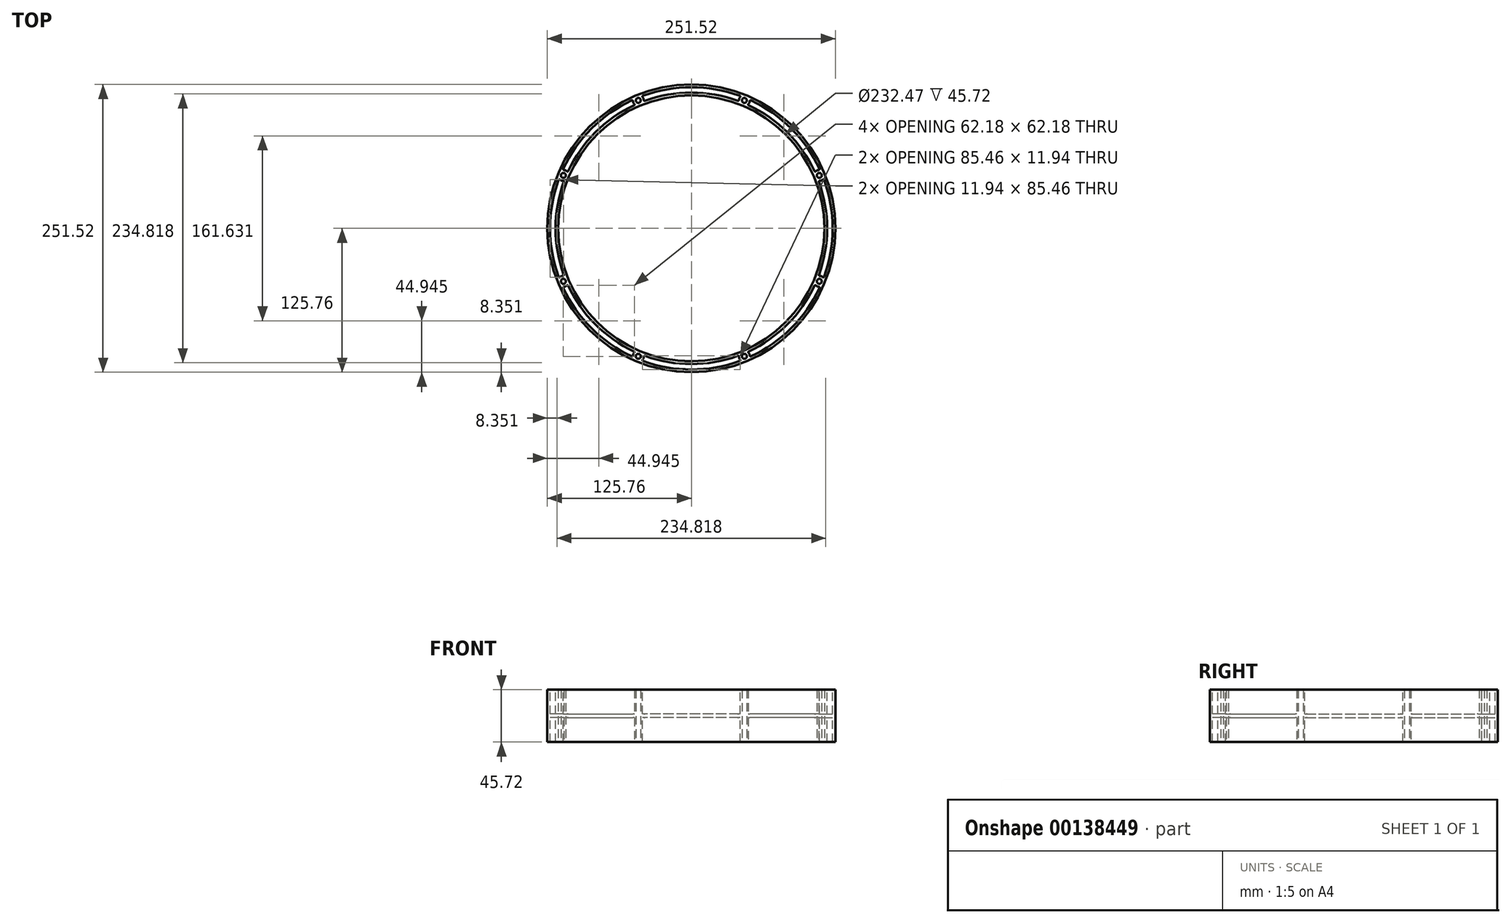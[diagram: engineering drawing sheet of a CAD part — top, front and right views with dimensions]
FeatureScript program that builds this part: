
annotation { "Feature Type Name" : "Feature", "Feature Type Description" : "" }
export const myFeature = defineFeature(function(context is Context, id is Id, definition is map)
    precondition{}
    {
        {
            var Q0;
            Q0=qCreatedBy(makeId("Top.planeOp"),FACE);
            var sketch = newSketch(context, id + "F0", { "sketchPlane" : qUnion([Q0])});
            skCircle(sketch, "E0", {"center": v(0, 0) * mm, "radius": 125.76 * mm});
            skCircle(sketch, "E1.cCircle", {"center": v(0, 0) * mm, "radius": 111.79 * mm, "construction": true});
            skLineSegment(sketch, "E1.0", {"start": v(46.3, -111.79) * mm, "end": v(-46.3, -111.79) * mm, "construction": true});
            skLineSegment(sketch, "E1.1", {"start": v(-46.3, -111.79) * mm, "end": v(-111.79, -46.3) * mm, "construction": true});
            skLineSegment(sketch, "E1.2", {"start": v(-111.79, -46.3) * mm, "end": v(-111.79, 46.3) * mm, "construction": true});
            skLineSegment(sketch, "E1.3", {"start": v(-111.79, 46.3) * mm, "end": v(-46.3, 111.79) * mm, "construction": true});
            skLineSegment(sketch, "E1.4", {"start": v(-46.3, 111.79) * mm, "end": v(46.3, 111.79) * mm, "construction": true});
            skLineSegment(sketch, "E1.5", {"start": v(46.3, 111.79) * mm, "end": v(111.79, 46.3) * mm, "construction": true});
            skLineSegment(sketch, "E1.6", {"start": v(111.79, 46.3) * mm, "end": v(111.79, -46.3) * mm, "construction": true});
            skLineSegment(sketch, "E1.7", {"start": v(111.79, -46.3) * mm, "end": v(46.3, -111.79) * mm, "construction": true});
            skCircle(sketch, "E2", {"center": v(-46.3, 111.79) * mm, "radius": 4.76 * mm, "construction": true});
            skCircle(sketch, "E3", {"center": v(0, 0) * mm, "radius": 116.24 * mm});
            skCircle(sketch, "E4", {"center": v(-46.3, 111.79) * mm, "radius": 2.15 * mm});
            skCircle(sketch, "E5", {"center": v(46.3, 111.79) * mm, "radius": 2.15 * mm});
            skCircle(sketch, "E6", {"center": v(111.79, 46.3) * mm, "radius": 2.15 * mm});
            skCircle(sketch, "E7", {"center": v(111.79, -46.3) * mm, "radius": 2.15 * mm});
            skCircle(sketch, "E8", {"center": v(46.3, -111.79) * mm, "radius": 2.15 * mm});
            skCircle(sketch, "E9", {"center": v(-46.3, -111.79) * mm, "radius": 2.15 * mm});
            skCircle(sketch, "E10", {"center": v(-111.79, -46.3) * mm, "radius": 2.15 * mm});
            skCircle(sketch, "E11", {"center": v(-111.79, 46.3) * mm, "radius": 2.15 * mm});
            skSolve(sketch);
        }
        {
            var Q0;
            Q0 = qSketchRegion(id + "F0", true);
            extrude(context, id + "F1", {"entities" : qUnion([Q0]), "depth" : 45.72 * mm});
        }
        {
            var Q0;
            Q0=makeQuery(id+"F1.opExtrude","CAP_FACE",FACE,{"disambiguationData":[OSD([sQuery(id+"F0.wireOp",EDGE,"E0"),sQuery(id+"F0.wireOp",EDGE,"E3"),sQuery(id+"F0.wireOp",EDGE,"E4"),sQuery(id+"F0.wireOp",EDGE,"E5"),sQuery(id+"F0.wireOp",EDGE,"E6"),sQuery(id+"F0.wireOp",EDGE,"E7"),sQuery(id+"F0.wireOp",EDGE,"E8"),sQuery(id+"F0.wireOp",EDGE,"E9"),sQuery(id+"F0.wireOp",EDGE,"E10"),sQuery(id+"F0.wireOp",EDGE,"E11")])],"isStart":false});
            var sketch = newSketch(context, id + "F2", { "sketchPlane" : qUnion([Q0])});
            skArc(sketch, "E12", {"start": v(-107.96, 49.14) * mm, "mid": v(-109.9, 50.67) * mm, "end": v(-112.33, 51.04) * mm});
            skArc(sketch, "E13", {"start": v(-49.14, 107.96) * mm, "mid": v(-83.88, 83.88) * mm, "end": v(-107.96, 49.14) * mm});
            skArc(sketch, "E14", {"start": v(-51.04, 112.33) * mm, "mid": v(-50.67, 109.9) * mm, "end": v(-49.14, 107.96) * mm});
            skArc(sketch, "E15", {"start": v(-51.04, 112.33) * mm, "mid": v(-87.24, 87.24) * mm, "end": v(-112.33, 51.04) * mm});
            skSolve(sketch);
        }
        {
            var Q0;
            Q0 = qSketchRegion(id + "F2", true);
            var Q1;
            Q1=makeQuery(id+"F1.opExtrude","CAP_FACE",FACE,{"disambiguationData":[OSD([sQuery(id+"F0.wireOp",EDGE,"E0"),sQuery(id+"F0.wireOp",EDGE,"E3"),sQuery(id+"F0.wireOp",EDGE,"E4"),sQuery(id+"F0.wireOp",EDGE,"E5"),sQuery(id+"F0.wireOp",EDGE,"E6"),sQuery(id+"F0.wireOp",EDGE,"E7"),sQuery(id+"F0.wireOp",EDGE,"E8"),sQuery(id+"F0.wireOp",EDGE,"E9"),sQuery(id+"F0.wireOp",EDGE,"E10"),sQuery(id+"F0.wireOp",EDGE,"E11")])],"isStart":true});
            extrude(context, id + "F3", {"entities" : qUnion([Q0]), "operationType" : NewBodyOperationType.REMOVE, "endBound" : BoundingType.UP_TO_SURFACE, "oppositeDirection" : true, "endBoundEntityFace" : qUnion([Q1]), "depth" : 25.4 * mm});
        }
        {
            var Q0;
            {var subQ0=sQuery(id+"F2.wireOp",EDGE,"E13");var subQ1=sQuery(id+"F2.wireOp",EDGE,"E14");Q0=makeQuery(id+"F8.boolean.opBoolean","SPLIT",EDGE,{"disambiguationData":[TD([makeQuery(id+"F1.opExtrude","CAP_FACE",FACE,{"disambiguationData":[OSD([sQuery(id+"F0.wireOp",EDGE,"E0"),sQuery(id+"F0.wireOp",EDGE,"E3"),sQuery(id+"F0.wireOp",EDGE,"E4"),sQuery(id+"F0.wireOp",EDGE,"E5"),sQuery(id+"F0.wireOp",EDGE,"E6"),sQuery(id+"F0.wireOp",EDGE,"E7"),sQuery(id+"F0.wireOp",EDGE,"E8"),sQuery(id+"F0.wireOp",EDGE,"E9"),sQuery(id+"F0.wireOp",EDGE,"E10"),sQuery(id+"F0.wireOp",EDGE,"E11")])],"isStart":false})])],"derivedFrom":makeQuery(id+"F3.boolean.opBoolean","COPY",EDGE,{"derivedFrom":makeQuery(id+"F3.opExtrude","SWEPT_EDGE",EDGE,{"disambiguationData":[OSD([subQ0,subQ1])]})})});}
            var Q1;
            {var subQ0=sQuery(id+"F2.wireOp",EDGE,"E14");var subQ1=sQuery(id+"F2.wireOp",EDGE,"E15");Q1=makeQuery(id+"F8.boolean.opBoolean","SPLIT",EDGE,{"disambiguationData":[TD([makeQuery(id+"F1.opExtrude","CAP_FACE",FACE,{"disambiguationData":[OSD([sQuery(id+"F0.wireOp",EDGE,"E0"),sQuery(id+"F0.wireOp",EDGE,"E3"),sQuery(id+"F0.wireOp",EDGE,"E4"),sQuery(id+"F0.wireOp",EDGE,"E5"),sQuery(id+"F0.wireOp",EDGE,"E6"),sQuery(id+"F0.wireOp",EDGE,"E7"),sQuery(id+"F0.wireOp",EDGE,"E8"),sQuery(id+"F0.wireOp",EDGE,"E9"),sQuery(id+"F0.wireOp",EDGE,"E10"),sQuery(id+"F0.wireOp",EDGE,"E11")])],"isStart":false})])],"derivedFrom":makeQuery(id+"F3.boolean.opBoolean","COPY",EDGE,{"derivedFrom":makeQuery(id+"F3.opExtrude","SWEPT_EDGE",EDGE,{"disambiguationData":[OSD([subQ0,subQ1])]})})});}
            var Q2;
            {var subQ0=sQuery(id+"F2.wireOp",EDGE,"E12");var subQ1=sQuery(id+"F2.wireOp",EDGE,"E13");Q2=makeQuery(id+"F8.boolean.opBoolean","SPLIT",EDGE,{"disambiguationData":[TD([makeQuery(id+"F1.opExtrude","CAP_FACE",FACE,{"disambiguationData":[OSD([sQuery(id+"F0.wireOp",EDGE,"E0"),sQuery(id+"F0.wireOp",EDGE,"E3"),sQuery(id+"F0.wireOp",EDGE,"E4"),sQuery(id+"F0.wireOp",EDGE,"E5"),sQuery(id+"F0.wireOp",EDGE,"E6"),sQuery(id+"F0.wireOp",EDGE,"E7"),sQuery(id+"F0.wireOp",EDGE,"E8"),sQuery(id+"F0.wireOp",EDGE,"E9"),sQuery(id+"F0.wireOp",EDGE,"E10"),sQuery(id+"F0.wireOp",EDGE,"E11")])],"isStart":false})])],"derivedFrom":makeQuery(id+"F3.boolean.opBoolean","COPY",EDGE,{"derivedFrom":makeQuery(id+"F3.opExtrude","SWEPT_EDGE",EDGE,{"disambiguationData":[OSD([subQ0,subQ1])]})})});}
            var Q3;
            {var subQ0=sQuery(id+"F2.wireOp",EDGE,"E12");var subQ1=sQuery(id+"F2.wireOp",EDGE,"E15");Q3=makeQuery(id+"F8.boolean.opBoolean","SPLIT",EDGE,{"disambiguationData":[TD([makeQuery(id+"F1.opExtrude","CAP_FACE",FACE,{"disambiguationData":[OSD([sQuery(id+"F0.wireOp",EDGE,"E0"),sQuery(id+"F0.wireOp",EDGE,"E3"),sQuery(id+"F0.wireOp",EDGE,"E4"),sQuery(id+"F0.wireOp",EDGE,"E5"),sQuery(id+"F0.wireOp",EDGE,"E6"),sQuery(id+"F0.wireOp",EDGE,"E7"),sQuery(id+"F0.wireOp",EDGE,"E8"),sQuery(id+"F0.wireOp",EDGE,"E9"),sQuery(id+"F0.wireOp",EDGE,"E10"),sQuery(id+"F0.wireOp",EDGE,"E11")])],"isStart":false})])],"derivedFrom":makeQuery(id+"F3.boolean.opBoolean","COPY",EDGE,{"derivedFrom":makeQuery(id+"F3.opExtrude","SWEPT_EDGE",EDGE,{"disambiguationData":[OSD([subQ0,subQ1])]})})});}
            fillet(context, id + "F4", {"entities" : qUnion([Q0, Q1, Q2, Q3]), "radius" : 0.76 * mm, "tangentPropagation" : true, "allowEdgeOverflow" : false});
        }
        {
            var Q0;
            Q0=makeQuery(id+"F4.opFillet","BLEND_FACE",FACE,{"disambiguationData":[OSD([sQuery(id+"F2.wireOp",EDGE,"E13"),sQuery(id+"F2.wireOp",EDGE,"E14")])]});
            var Q1;
            Q1=makeQuery(id+"F3.boolean.opBoolean","COPY",FACE,{"derivedFrom":makeQuery(id+"F3.opExtrude","SWEPT_FACE",FACE,{"disambiguationData":[OSD([sQuery(id+"F2.wireOp",EDGE,"E14")])]})});
            var Q2;
            Q2=makeQuery(id+"F4.opFillet","BLEND_FACE",FACE,{"disambiguationData":[OSD([sQuery(id+"F2.wireOp",EDGE,"E14"),sQuery(id+"F2.wireOp",EDGE,"E15")])]});
            var Q3;
            Q3=makeQuery(id+"F3.boolean.opBoolean","COPY",FACE,{"derivedFrom":makeQuery(id+"F3.opExtrude","SWEPT_FACE",FACE,{"disambiguationData":[OSD([sQuery(id+"F2.wireOp",EDGE,"E15")])]})});
            var Q4;
            Q4=makeQuery(id+"F3.boolean.opBoolean","COPY",FACE,{"derivedFrom":makeQuery(id+"F3.opExtrude","SWEPT_FACE",FACE,{"disambiguationData":[OSD([sQuery(id+"F2.wireOp",EDGE,"E13")])]})});
            var Q5;
            Q5=makeQuery(id+"F4.opFillet","BLEND_FACE",FACE,{"disambiguationData":[OSD([sQuery(id+"F2.wireOp",EDGE,"E12"),sQuery(id+"F2.wireOp",EDGE,"E13")])]});
            var Q6;
            Q6=makeQuery(id+"F3.boolean.opBoolean","COPY",FACE,{"derivedFrom":makeQuery(id+"F3.opExtrude","SWEPT_FACE",FACE,{"disambiguationData":[OSD([sQuery(id+"F2.wireOp",EDGE,"E12")])]})});
            var Q7;
            Q7=makeQuery(id+"F4.opFillet","BLEND_FACE",FACE,{"disambiguationData":[OSD([sQuery(id+"F2.wireOp",EDGE,"E12"),sQuery(id+"F2.wireOp",EDGE,"E15")])]});
            var Q8;
            Q8=makeQuery(id+"F1.opExtrude","SWEPT_FACE",FACE,{"disambiguationData":[OSD([sQuery(id+"F0.wireOp",EDGE,"E3")])]});
            circularPattern(context, id + "F5", {"patternType" : PatternType.FACE, "faces" : qUnion([Q0, Q1, Q2, Q3, Q4, Q5, Q6, Q7]), "axis" : qUnion([Q8]), "angle" : 45 * degree, "instanceCount" : 8});
        }
        {
            var Q0;
            Q0=makeQuery(id+"F1.opExtrude","CAP_FACE",FACE,{"disambiguationData":[OSD([sQuery(id+"F0.wireOp",EDGE,"E0"),sQuery(id+"F0.wireOp",EDGE,"E3"),sQuery(id+"F0.wireOp",EDGE,"E4"),sQuery(id+"F0.wireOp",EDGE,"E5"),sQuery(id+"F0.wireOp",EDGE,"E6"),sQuery(id+"F0.wireOp",EDGE,"E7"),sQuery(id+"F0.wireOp",EDGE,"E8"),sQuery(id+"F0.wireOp",EDGE,"E9"),sQuery(id+"F0.wireOp",EDGE,"E10"),sQuery(id+"F0.wireOp",EDGE,"E11")])],"isStart":false});
            cPlane(context, id + "F6", {"entities" : qUnion([Q0]), "cplaneType" : CPlaneType.OFFSET, "offset" : 22.86 * mm, "oppositeDirection" : true, "width" : 152.4 * mm, "height" : 152.4 * mm});
        }
        {
            var Q0;
            Q0=qCreatedBy(id+"F6.planeOp",FACE);
            var sketch = newSketch(context, id + "F7", { "sketchPlane" : qUnion([Q0])});
            skCircle(sketch, "E16", {"center": v(0, 0) * mm, "radius": 125.76 * mm});
            skCircle(sketch, "E17", {"center": v(0, 0) * mm, "radius": 116.24 * mm});
            skCircle(sketch, "E18", {"center": v(-46.3, 111.79) * mm, "radius": 2.15 * mm});
            skCircle(sketch, "E19", {"center": v(46.3, 111.79) * mm, "radius": 2.15 * mm});
            skCircle(sketch, "E20", {"center": v(111.79, 46.3) * mm, "radius": 2.15 * mm});
            skCircle(sketch, "E21", {"center": v(-46.3, -111.79) * mm, "radius": 2.15 * mm});
            skCircle(sketch, "E22", {"center": v(111.79, -46.3) * mm, "radius": 2.15 * mm});
            skCircle(sketch, "E23", {"center": v(46.3, -111.79) * mm, "radius": 2.15 * mm});
            skCircle(sketch, "E24", {"center": v(-111.79, -46.3) * mm, "radius": 2.15 * mm});
            skCircle(sketch, "E25", {"center": v(-111.79, 46.3) * mm, "radius": 2.15 * mm});
            skSolve(sketch);
        }
        {
            var Q0;
            Q0 = qSketchRegion(id + "F7", true);
            extrude(context, id + "F8", {"entities" : qUnion([Q0]), "operationType" : NewBodyOperationType.ADD, "endBound" : BoundingType.SYMMETRIC, "depth" : 3.17 * mm});
        }
    });
